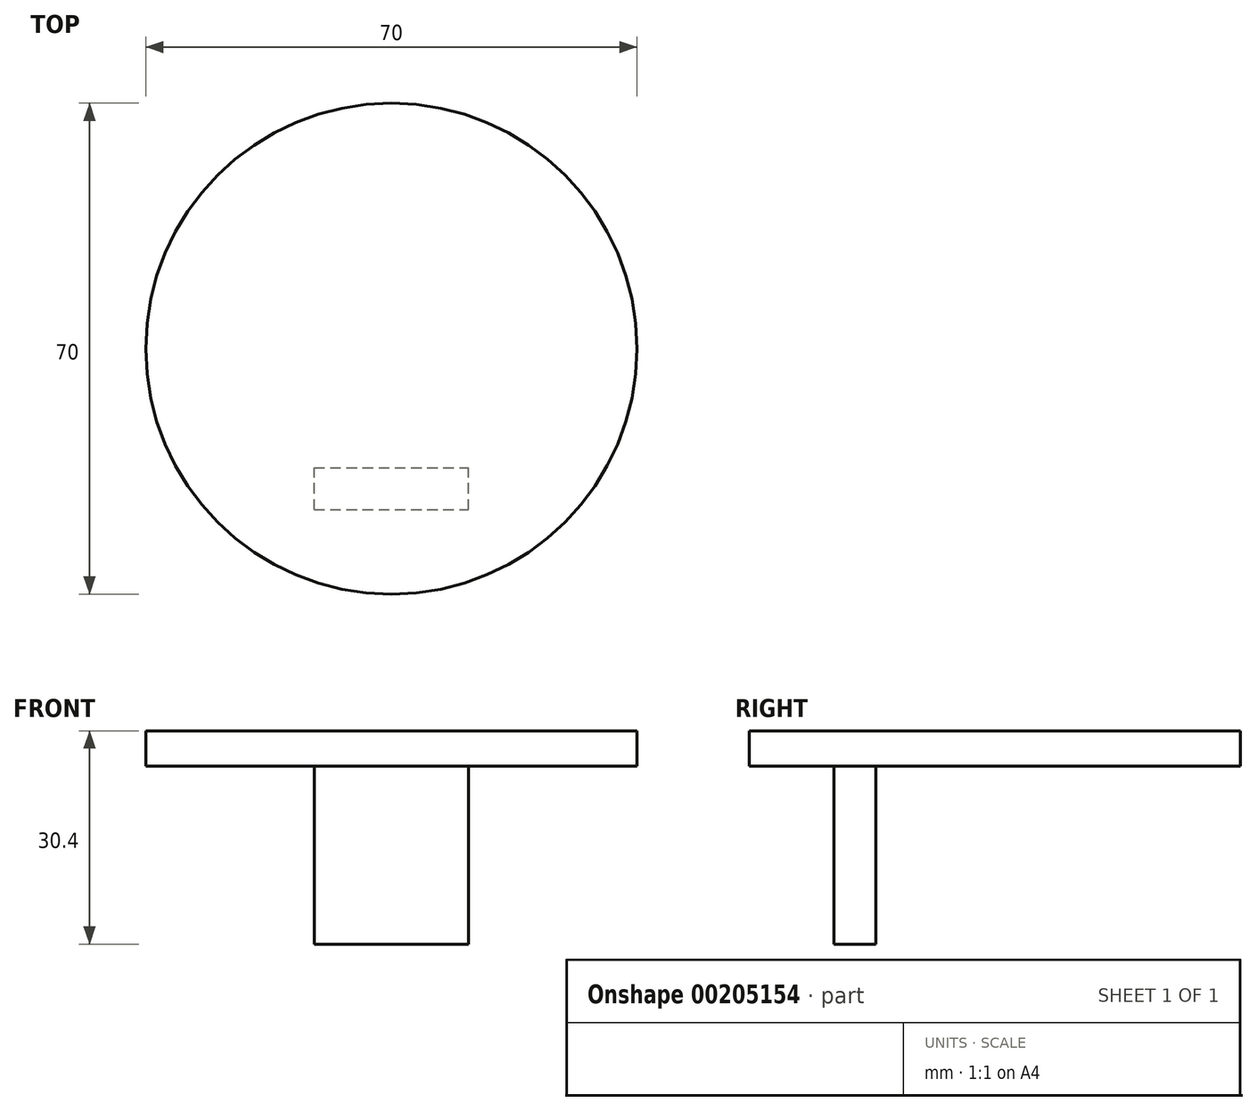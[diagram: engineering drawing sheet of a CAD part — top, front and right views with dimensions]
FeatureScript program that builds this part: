
annotation { "Feature Type Name" : "Feature", "Feature Type Description" : "" }
export const myFeature = defineFeature(function(context is Context, id is Id, definition is map)
    precondition{}
    {
        {
            var Q0;
            Q0=qCreatedBy(makeId("Top.planeOp"),FACE);
            var sketch = newSketch(context, id + "F0", { "sketchPlane" : qUnion([Q0])});
            skCircle(sketch, "E0", {"center": v(0, 0) * mm, "radius": 35 * mm});
            skSolve(sketch);
        }
        {
            var Q0;
            Q0 = qSketchRegion(id + "F0", true);
            extrude(context, id + "F1", {"entities" : qUnion([Q0]), "depth" : 5 * mm});
        }
        {
            var Q0;
            Q0=makeQuery(id+"F1.opExtrude","CAP_FACE",FACE,{"disambiguationData":[OSD([sQuery(id+"F0.wireOp",EDGE,"E0")])],"isStart":true});
            var sketch = newSketch(context, id + "F2", { "sketchPlane" : qUnion([Q0])});
            skLineSegment(sketch, "E1.bottom", {"start": v(-11, 22.96) * mm, "end": v(11, 22.96) * mm});
            skLineSegment(sketch, "E1.top", {"start": v(-11, 16.96) * mm, "end": v(11, 16.96) * mm});
            skLineSegment(sketch, "E1.left", {"start": v(-11, 22.96) * mm, "end": v(-11, 16.96) * mm});
            skLineSegment(sketch, "E1.right", {"start": v(11, 22.96) * mm, "end": v(11, 16.96) * mm});
            skPoint(sketch, "E1.middle", {"position": v(0, 19.96) * mm});
            skSolve(sketch);
        }
        {
            var Q0;
            Q0 = qSketchRegion(id + "F2", true);
            extrude(context, id + "F3", {"entities" : qUnion([Q0]), "operationType" : NewBodyOperationType.ADD, "depth" : 25.4 * mm});
        }
    });
